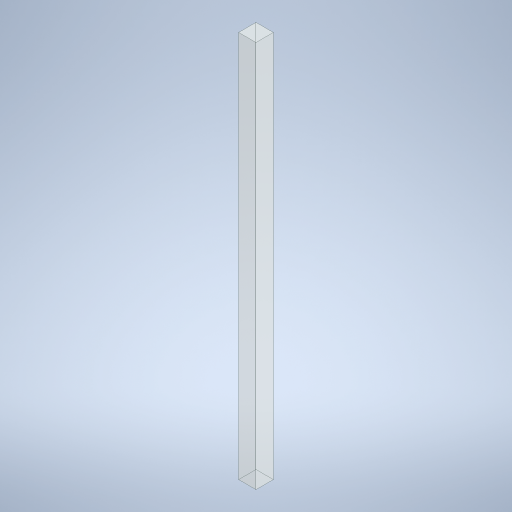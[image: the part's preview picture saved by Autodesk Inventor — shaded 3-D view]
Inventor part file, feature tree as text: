
AUTODESK INVENTOR PART (.ipt)
format: ipt  version: 2024 (Build 280153000, 153)  size: 236,032 bytes
history: native  units: in
note: dims shown in document units (in); Inventor stores cm internally (conversion verified against a paired STEP export)
features: extrude x1, sketch x1
ambient origin geometry x8: Origin, YZ Plane, XZ Plane, XY Plane, X Axis, Y Axis, Z Axis, Center Point
bodies: Solid1 (feature_tree)
feature tree (2):
  extrude  "Extrusion1"  Depth=16.0in
  sketch  "Sketch1"  dims[d1=16.0in d2=16.0in d3=356.25in d4=0.0in]
